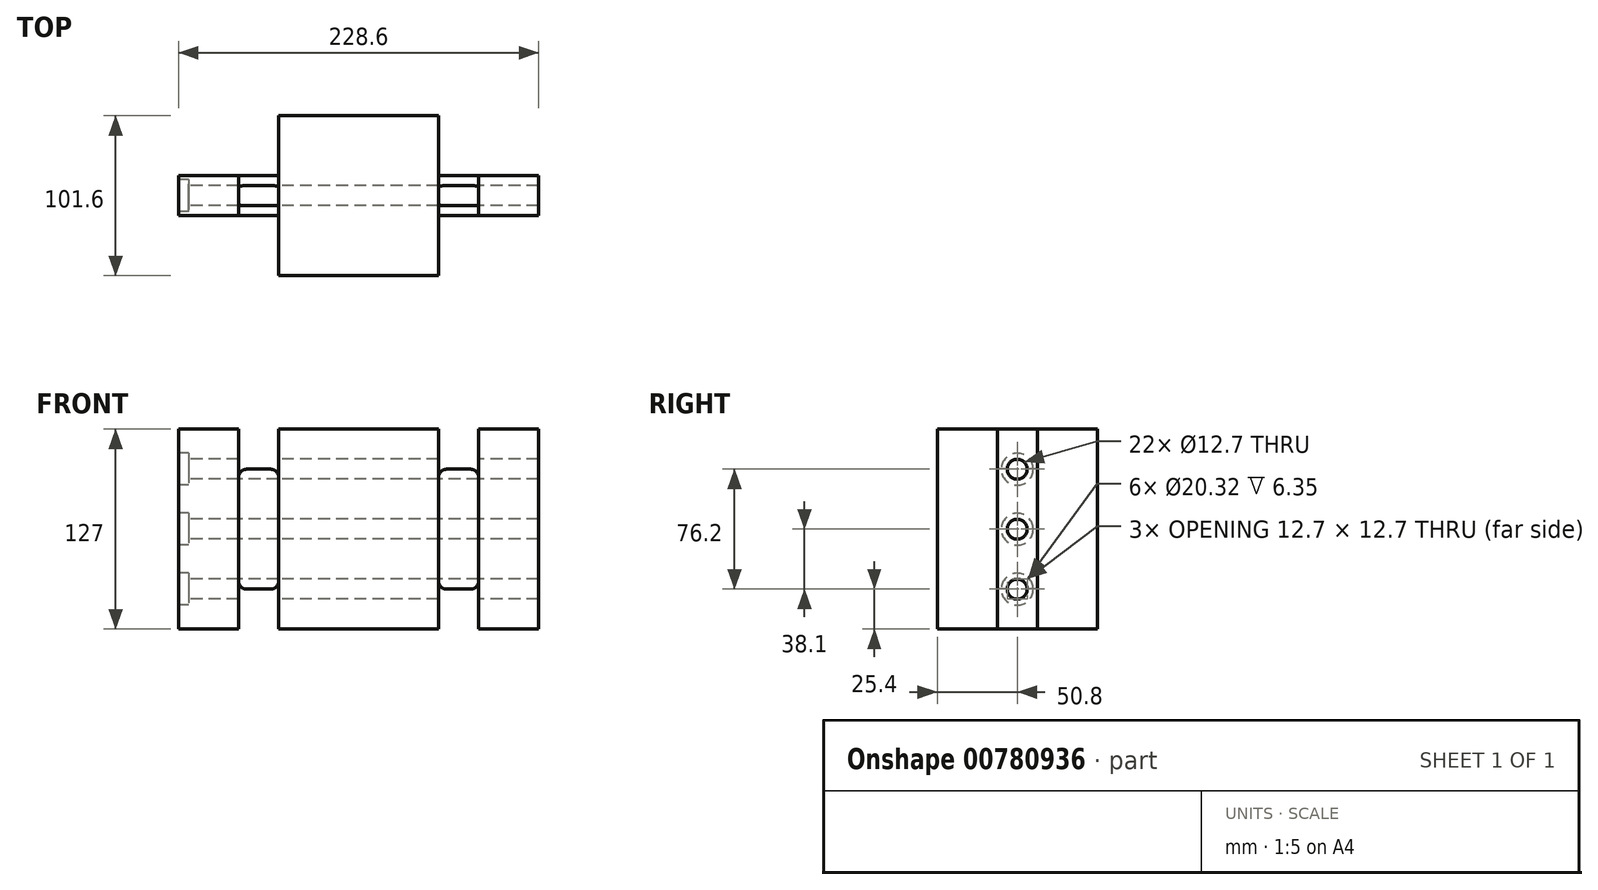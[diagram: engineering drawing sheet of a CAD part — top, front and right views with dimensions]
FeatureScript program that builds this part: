
annotation { "Feature Type Name" : "Feature", "Feature Type Description" : "" }
export const myFeature = defineFeature(function(context is Context, id is Id, definition is map)
    precondition{}
    {
        {
            var Q0;
            Q0=qCreatedBy(makeId("Top.planeOp"),FACE);
            var sketch = newSketch(context, id + "F0", { "sketchPlane" : qUnion([Q0])});
            skLineSegment(sketch, "E0.bottom", {"start": v(50.8, 50.8) * mm, "end": v(-50.8, 50.8) * mm});
            skLineSegment(sketch, "E0.top", {"start": v(50.8, -50.8) * mm, "end": v(-50.8, -50.8) * mm});
            skLineSegment(sketch, "E0.left", {"start": v(50.8, 50.8) * mm, "end": v(50.8, -50.8) * mm});
            skLineSegment(sketch, "E0.right", {"start": v(-50.8, 50.8) * mm, "end": v(-50.8, -50.8) * mm});
            skPoint(sketch, "E0.middle", {"position": v(0, 0) * mm});
            skLineSegment(sketch, "E1.bottom", {"start": v(114.3, 12.7) * mm, "end": v(76.2, 12.7) * mm});
            skLineSegment(sketch, "E1.top", {"start": v(114.3, -12.7) * mm, "end": v(76.2, -12.7) * mm});
            skLineSegment(sketch, "E1.left", {"start": v(114.3, 12.7) * mm, "end": v(114.3, -12.7) * mm});
            skLineSegment(sketch, "E1.right", {"start": v(76.2, 12.7) * mm, "end": v(76.2, -12.7) * mm});
            skPoint(sketch, "E1.middle", {"position": v(95.25, 0) * mm});
            skLineSegment(sketch, "E2.MirrorCS", {"start": v(-76.2, 12.7) * mm, "end": v(-76.2, -12.7) * mm});
            skLineSegment(sketch, "E3.MirrorCS", {"start": v(-114.3, 12.7) * mm, "end": v(-76.2, 12.7) * mm});
            skLineSegment(sketch, "E4.MirrorCS", {"start": v(-114.3, 12.7) * mm, "end": v(-114.3, -12.7) * mm});
            skLineSegment(sketch, "E5.MirrorCS", {"start": v(-114.3, -12.7) * mm, "end": v(-76.2, -12.7) * mm});
            skPoint(sketch, "E6.MirrorP", {"position": v(-95.25, 0) * mm});
            skLineSegment(sketch, "E7", {"start": v(-76.2, 12.7) * mm, "end": v(-50.8, 12.7) * mm});
            skLineSegment(sketch, "E8", {"start": v(-76.2, -12.7) * mm, "end": v(-50.8, -12.7) * mm});
            skLineSegment(sketch, "E9", {"start": v(76.2, 12.7) * mm, "end": v(50.8, 12.7) * mm});
            skLineSegment(sketch, "E10", {"start": v(76.2, -12.7) * mm, "end": v(50.8, -12.7) * mm});
            skSolve(sketch);
        }
        {
            var Q0;
            Q0=makeQuery(id+"F0.imprint","IMPRINT",FACE,{"disambiguationData":[TD([[makeQuery(id+"F0.imprint","IMPRINT",EDGE,{"derivedFrom":sQuery(id+"F0.wireOp",EDGE,"E2.MirrorCS")}),-1.0]])]});
            var Q1;
            {var subQ3=sQuery(id+"F0.wireOp",EDGE,"E0.bottom");Q1=makeQuery(id+"F0.imprint","IMPRINT",FACE,{"disambiguationData":[TD([[makeQuery(id+"F0.imprint","IMPRINT",EDGE,{"derivedFrom":subQ3}),1.0]])]});}
            var Q2;
            Q2=makeQuery(id+"F0.imprint","IMPRINT",FACE,{"disambiguationData":[TD([[makeQuery(id+"F0.imprint","IMPRINT",EDGE,{"derivedFrom":sQuery(id+"F0.wireOp",EDGE,"E1.bottom")}),1.0]])]});
            extrude(context, id + "F1", {"entities" : qUnion([Q0, Q1, Q2]), "endBound" : BoundingType.SYMMETRIC, "depth" : 127 * mm, "offsetDistance" : 25.4 * mm});
        }
        {
            var Q0;
            Q0=makeQuery(id+"F0.imprint","IMPRINT",FACE,{"disambiguationData":[TD([[makeQuery(id+"F0.imprint","IMPRINT",EDGE,{"derivedFrom":sQuery(id+"F0.wireOp",EDGE,"E2.MirrorCS")}),1.0]])]});
            var Q1;
            Q1=makeQuery(id+"F0.imprint","IMPRINT",FACE,{"disambiguationData":[TD([[makeQuery(id+"F0.imprint","IMPRINT",EDGE,{"derivedFrom":sQuery(id+"F0.wireOp",EDGE,"E1.right")}),-1.0]])]});
            extrude(context, id + "F2", {"entities" : qUnion([Q0, Q1]), "endBound" : BoundingType.SYMMETRIC, "depth" : 76.2 * mm, "offsetDistance" : 25.4 * mm});
        }
        {
            var Q0;
            Q0=makeQuery(id+"F2.opExtrude","CAP_EDGE",EDGE,{"disambiguationData":[OSD([sQuery(id+"F0.wireOp",EDGE,"E2.MirrorCS")])],"isStart":false});
            var Q1;
            Q1=makeQuery(id+"F2.opExtrude","CAP_EDGE",EDGE,{"disambiguationData":[OSD([sQuery(id+"F0.wireOp",EDGE,"E0.right")])],"isStart":false});
            var Q2;
            Q2=makeQuery(id+"F2.opExtrude","CAP_EDGE",EDGE,{"disambiguationData":[OSD([sQuery(id+"F0.wireOp",EDGE,"E1.right")])],"isStart":false});
            var Q3;
            Q3=makeQuery(id+"F2.opExtrude","CAP_EDGE",EDGE,{"disambiguationData":[OSD([sQuery(id+"F0.wireOp",EDGE,"E0.left")])],"isStart":false});
            var Q4;
            Q4=makeQuery(id+"F2.opExtrude","CAP_EDGE",EDGE,{"disambiguationData":[OSD([sQuery(id+"F0.wireOp",EDGE,"E2.MirrorCS")])],"isStart":true});
            var Q5;
            Q5=makeQuery(id+"F2.opExtrude","CAP_EDGE",EDGE,{"disambiguationData":[OSD([sQuery(id+"F0.wireOp",EDGE,"E0.left")])],"isStart":true});
            var Q6;
            Q6=makeQuery(id+"F2.opExtrude","CAP_EDGE",EDGE,{"disambiguationData":[OSD([sQuery(id+"F0.wireOp",EDGE,"E1.right")])],"isStart":true});
            var Q7;
            Q7=makeQuery(id+"F2.opExtrude","CAP_EDGE",EDGE,{"disambiguationData":[OSD([sQuery(id+"F0.wireOp",EDGE,"E0.right")])],"isStart":true});
            fillet(context, id + "F3", {"entities" : qUnion([Q0, Q1, Q2, Q3, Q4, Q5, Q6, Q7]), "radius" : 5.08 * mm, "tangentPropagation" : true, "allowEdgeOverflow" : false});
        }
        {
            var Q0;
            Q0=makeQuery(id+"F1.opExtrude","SWEPT_FACE",FACE,{"disambiguationData":[OSD([sQuery(id+"F0.wireOp",EDGE,"E4.MirrorCS")])]});
            var sketch = newSketch(context, id + "F4", { "sketchPlane" : qUnion([Q0])});
            skCircle(sketch, "E11", {"center": v(0, 0) * mm, "radius": 9.53 * mm});
            skCircle(sketch, "E12", {"center": v(0, -38.1) * mm, "radius": 6.35 * mm});
            skCircle(sketch, "E13.MirrorC", {"center": v(0, 38.1) * mm, "radius": 6.35 * mm});
            skSolve(sketch);
        }
        {
            var Q0;
            Q0=sQuery(id+"F4.wireOp",VERTEX,"E13.MirrorC.center");
            var Q1;
            Q1=sQuery(id+"F4.wireOp",VERTEX,"E12.center");
            var Q2;
            Q2=sQuery(id+"F4.wireOp",VERTEX,"E11.center");
            var Q3;
            Q3=makeQuery(id+"F2.opExtrude","SWEPT_BODY",BODY,{"disambiguationData":[OSD([sQuery(id+"F0.wireOp",EDGE,"E0.right"),sQuery(id+"F0.wireOp",EDGE,"E2.MirrorCS"),sQuery(id+"F0.wireOp",EDGE,"E7"),sQuery(id+"F0.wireOp",EDGE,"E8")])]});
            var Q4;
            Q4=makeQuery(id+"F2.opExtrude","SWEPT_BODY",BODY,{"disambiguationData":[OSD([sQuery(id+"F0.wireOp",EDGE,"E0.left"),sQuery(id+"F0.wireOp",EDGE,"E1.right"),sQuery(id+"F0.wireOp",EDGE,"E9"),sQuery(id+"F0.wireOp",EDGE,"E10")])]});
            var Q5;
            Q5=makeQuery(id+"F1.opExtrude","SWEPT_BODY",BODY,{"disambiguationData":[OSD([sQuery(id+"F0.wireOp",EDGE,"E0.bottom"),sQuery(id+"F0.wireOp",EDGE,"E0.top"),sQuery(id+"F0.wireOp",EDGE,"E0.left"),sQuery(id+"F0.wireOp",EDGE,"E0.right")])]});
            var Q6;
            Q6=makeQuery(id+"F1.opExtrude","SWEPT_BODY",BODY,{"disambiguationData":[OSD([sQuery(id+"F0.wireOp",EDGE,"E1.bottom"),sQuery(id+"F0.wireOp",EDGE,"E1.top"),sQuery(id+"F0.wireOp",EDGE,"E1.left"),sQuery(id+"F0.wireOp",EDGE,"E1.right")])]});
            var Q7;
            Q7=makeQuery(id+"F1.opExtrude","SWEPT_BODY",BODY,{"disambiguationData":[OSD([sQuery(id+"F0.wireOp",EDGE,"E2.MirrorCS"),sQuery(id+"F0.wireOp",EDGE,"E3.MirrorCS"),sQuery(id+"F0.wireOp",EDGE,"E4.MirrorCS"),sQuery(id+"F0.wireOp",EDGE,"E5.MirrorCS")])]});
            hole(context, id + "F5", {"style" : HoleStyle.C_BORE, "endStyle" : HoleEndStyle.THROUGH, "holeDiameter" : 12.7 * mm, "cBoreDiameter" : 20.32 * mm, "cBoreDepth" : 6.35 * mm, "majorDiameter" : 6.35 * mm, "isTappedThrough" : true, "tappedDepth" : 12.7 * mm, "tapClearance" : 3, "locations" : qUnion([Q0, Q1, Q2]), "scope" : qUnion([Q3, Q4, Q5, Q6, Q7])});
        }
    });
